# Revit family: Sanitary_Installation-Systems_Hansgrohe_01500XXX-iBox-universal-2-Basic-set_NEW
name_source: partatom
category: Plumbing Fixtures
revit_build: Autodesk Revit 2018 (Build: 20170223_1515(x64)
units: mm (PartAtom-declared; Revit-internal decimal feet)

## family parameters
Always vertical = No
Cut with Voids When Loaded = No
OmniClass Number = 23.31.11.19.11
OmniClass Title = Thermostatically Controlled Faucet Mixing Valves
Part Type = Normal
Room Calculation Point = No
Round Connector Dimension = Use Diameter
Shared = No
Work Plane-Based = Yes

## types (1)
- 01500XXX iBox universal 2 Basic set
    Always visible = Yes
    BIMobject category = Installation Systems
    Connector Description = Water Inlet 12.7 mm
    Default Elevation = 1219.2 mm  [stored 4 ft]
    Description = iBox universal 2 Basic set
    Design country = Germany
    Diameter = 13 mm
    EAN code = 4059625316900
    Edition number = 1
    IFC Classification = Sanitary Terminal
    Manufacturer = Hansgrohe
    Manufacturer country = Germany
    Manufacturer name = hansgrohe
    Material 1 = Hansgrohe - Plastic - Black
    Material 2 = Hansgrohe - Plastic - Light Green
    Material 3 = Hansgrohe - Plastic - Green
    Material 4 = Hansgrohe - Metal - Brass
    Model = 01500XXX
    OmniClass Code = 23-27 31 29 11
    OmniClass Description = Manual Mixing Valves
    Outlet Connector Description = Water Outlet 12.7 mm
    Outlet Diameter = 13 mm
    Product Guid = 7e5355e0-4ef9-4587-8d69-c027b1ae8319
    Product SKU = 01500XXX
    Product data url = https://bimobject.com
    Product group = Concealed Basic set bath/shower mixers
    Product name = 01500XXX iBox universal 2 Basic set
    Product url = https://pro.hansgrohe.com
    QR code = https://bimobject.com
    UNSPSC Code = 3018
    URL = https://www.hansgrohe.com
    Weight Net (Kg) = 1.7

note: [stored X ft] marks values corroborated as IEEE doubles in the binary element streams (Revit-internal decimal feet)

## geometry (parser evidence)
native form markers: Sweep x1
no freeform markers — native parametric forms only
